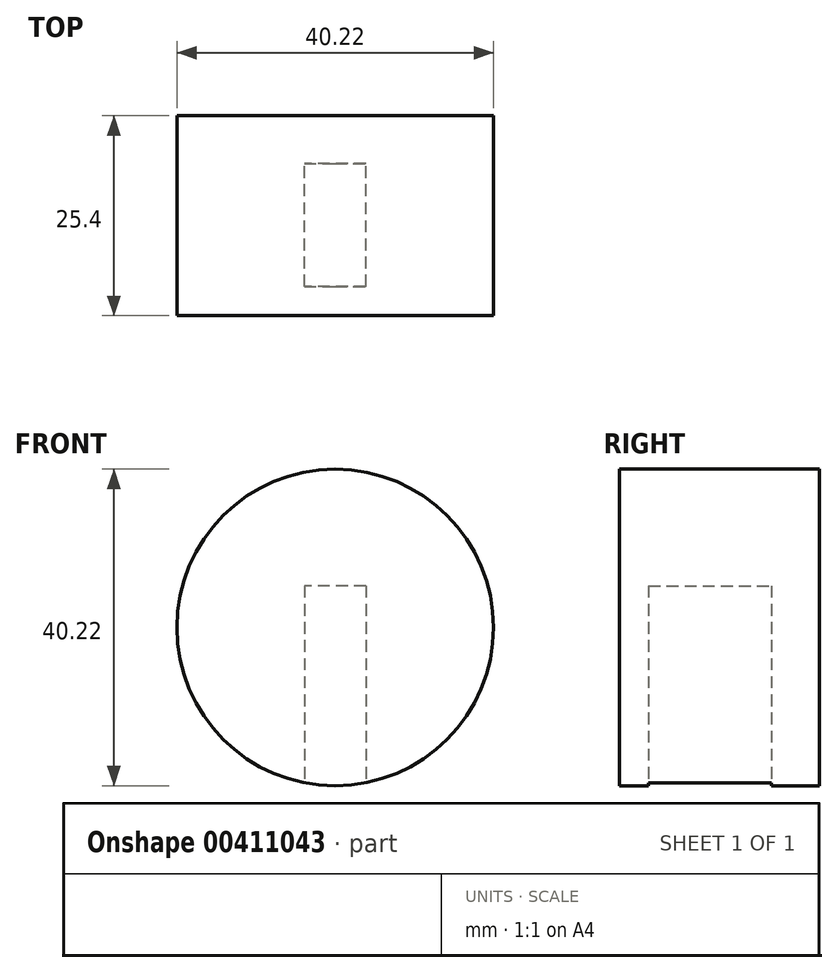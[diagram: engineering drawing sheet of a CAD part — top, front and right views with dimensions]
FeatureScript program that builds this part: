
annotation { "Feature Type Name" : "Feature", "Feature Type Description" : "" }
export const myFeature = defineFeature(function(context is Context, id is Id, definition is map)
    precondition{}
    {
        {
            var Q0;
            Q0=makeQuery(id+"FpqXDQrRn4MtqIi_0.opExtrude","CAP_FACE",FACE,{"disambiguationData":[OSD([sQuery(id+"Firfklal3LXNjvh_0.wireOp",EDGE,"oUQnCDGI-z4fQ-Nrtp-axCl-hYZYo9IPfIrT")])],"isStart":true});
            var sketch = newSketch(context, id + "F0", { "sketchPlane" : qUnion([Q0])});
            skCircle(sketch, "E0", {"center": v(0, 0) * mm, "radius": 16.6 * mm});
            skSolve(sketch);
        }
        {
            var Q0;
            Q0=qCreatedBy(makeId("Front.planeOp"),FACE);
            var sketch = newSketch(context, id + "F1", { "sketchPlane" : qUnion([Q0])});
            skPoint(sketch, "E1.first.point", {"position": v(0, 0) * mm});
            skPoint(sketch, "E1.second.point", {"position": v(4.7, 50.2) * mm});
            skPoint(sketch, "E2.first.point", {"position": v(-26.18, -75.14) * mm});
            skCircle(sketch, "E3", {"center": v(0, 20.11) * mm, "radius": 20.11 * mm});
            skSolve(sketch);
        }
        {
            var Q0;
            Q0 = qSketchRegion(id + "F1", true);
            var Q1;
            Q1=makeQuery(id+"F1.imprint","IMPRINT",FACE,{"disambiguationData":[TD([[makeQuery(id+"F1.imprint","IMPRINT",EDGE,{"derivedFrom":sQuery(id+"F1.wireOp",EDGE,"E3")}),1.0]])]});
            extrude(context, id + "F2", {"entities" : qUnion([Q0, Q1]), "depth" : 25.4 * mm});
        }
        {
            var Q0;
            Q0=qCreatedBy(makeId("Top.planeOp"),FACE);
            var sketch = newSketch(context, id + "F3", { "sketchPlane" : qUnion([Q0])});
            skLineSegment(sketch, "E4.bottom", {"start": v(3.9, -21.7) * mm, "end": v(-3.9, -21.7) * mm});
            skLineSegment(sketch, "E4.top", {"start": v(3.9, -6.08) * mm, "end": v(-3.9, -6.08) * mm});
            skLineSegment(sketch, "E4.left", {"start": v(3.9, -21.7) * mm, "end": v(3.9, -6.08) * mm});
            skLineSegment(sketch, "E4.right", {"start": v(-3.9, -21.7) * mm, "end": v(-3.9, -6.08) * mm});
            skPoint(sketch, "E4.middle", {"position": v(0, -13.89) * mm});
            skSolve(sketch);
        }
        {
            var Q0;
            Q0 = qSketchRegion(id + "F3", true);
            extrude(context, id + "F4", {"entities" : qUnion([Q0]), "operationType" : NewBodyOperationType.REMOVE, "depth" : 25.4 * mm});
        }
    });
